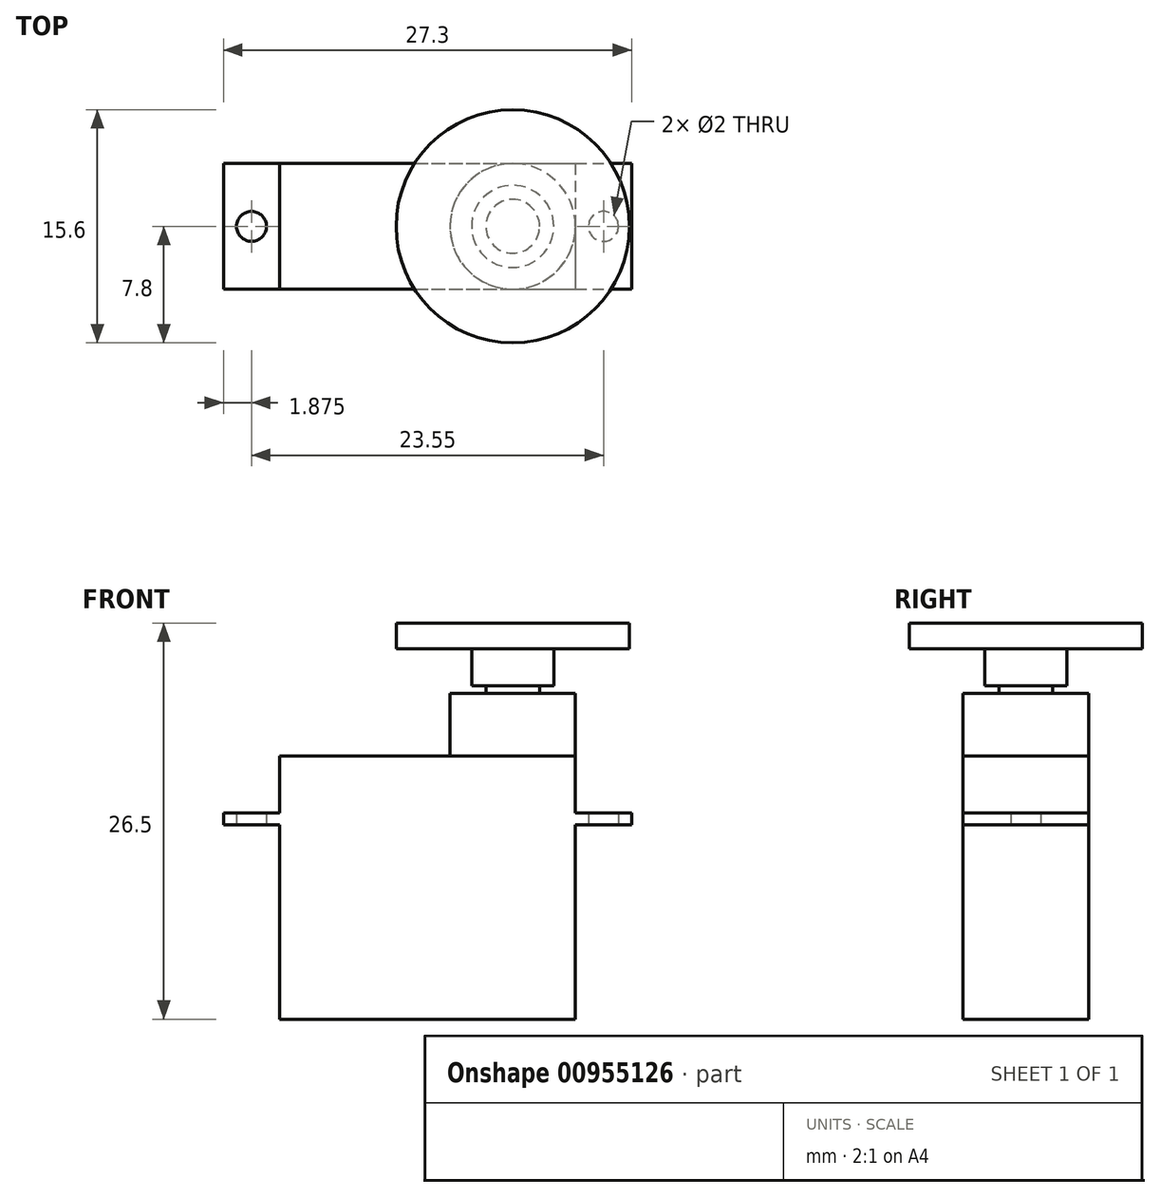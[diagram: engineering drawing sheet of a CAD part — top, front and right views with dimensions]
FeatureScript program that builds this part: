
annotation { "Feature Type Name" : "Feature", "Feature Type Description" : "" }
export const myFeature = defineFeature(function(context is Context, id is Id, definition is map)
    precondition{}
    {
        {
            var Q0;
            Q0=qCreatedBy(makeId("Top.planeOp"),FACE);
            var sketch = newSketch(context, id + "F0", { "sketchPlane" : qUnion([Q0])});
            skLineSegment(sketch, "E0.bottom", {"start": v(-15.6, 4.2) * mm, "end": v(4.2, 4.2) * mm});
            skLineSegment(sketch, "E0.top", {"start": v(-15.6, -4.2) * mm, "end": v(4.2, -4.2) * mm});
            skLineSegment(sketch, "E0.left", {"start": v(-15.6, 4.2) * mm, "end": v(-15.6, -4.2) * mm});
            skLineSegment(sketch, "E0.right", {"start": v(4.2, 4.2) * mm, "end": v(4.2, -4.2) * mm});
            skCircle(sketch, "E1", {"center": v(0, 0) * mm, "radius": 4.2 * mm});
            skCircle(sketch, "E2", {"center": v(0, 0) * mm, "radius": 1.8 * mm});
            skLineSegment(sketch, "E3.bottom", {"start": v(-15.6, 4.2) * mm, "end": v(-19.35, 4.2) * mm});
            skLineSegment(sketch, "E3.top", {"start": v(-15.6, -4.2) * mm, "end": v(-19.35, -4.2) * mm});
            skLineSegment(sketch, "E4", {"start": v(-5.7, 9.97) * mm, "end": v(-5.7, -15.7) * mm, "construction": true});
            skPoint(sketch, "E4.startSnap0", {"position": v(-5.7, 4.2) * mm});
            skLineSegment(sketch, "E5", {"start": v(-19.35, 4.2) * mm, "end": v(-19.35, -4.2) * mm});
            skCircle(sketch, "E6", {"center": v(-17.48, 0) * mm, "radius": 1 * mm});
            skLineSegment(sketch, "E7.MirrorCS", {"start": v(4.2, -4.2) * mm, "end": v(7.95, -4.2) * mm});
            skCircle(sketch, "E8.MirrorC", {"center": v(6.07, 0) * mm, "radius": 1 * mm});
            skLineSegment(sketch, "E9.MirrorCS", {"start": v(4.2, 4.2) * mm, "end": v(7.95, 4.2) * mm});
            skLineSegment(sketch, "E10.MirrorCS", {"start": v(7.95, 4.2) * mm, "end": v(7.95, -4.2) * mm});
            skSolve(sketch);
        }
        {
            var Q0;
            {var subQ0=sQuery(id+"F0.wireOp",EDGE,"E0.left");Q0=makeQuery(id+"F0.imprint","IMPRINT",FACE,{"disambiguationData":[TD([[makeQuery(id+"F0.imprint","IMPRINT",EDGE,{"derivedFrom":subQ0}),1.0]])]});}
            var Q1;
            Q1=makeQuery(id+"F0.imprint","IMPRINT",FACE,{"disambiguationData":[TD([[makeQuery(id+"F0.imprint","IMPRINT",EDGE,{"derivedFrom":sQuery(id+"F0.wireOp",EDGE,"E2")}),-1.0]])]});
            var Q2;
            Q2=makeQuery(id+"F0.imprint","IMPRINT",FACE,{"disambiguationData":[TD([[makeQuery(id+"F0.imprint","IMPRINT",EDGE,{"derivedFrom":sQuery(id+"F0.wireOp",EDGE,"E2")}),1.0]])]});
            var Q3;
            {var subQ1=sQuery(id+"F0.wireOp",EDGE,"E0.bottom");var subQ3=sQuery(id+"F0.wireOp",EDGE,"E1");var subQ4=makeQuery(id+"F0.imprint","INTERSECT",VERTEX,{"derivedFrom":[subQ1,subQ3]});Q3=makeQuery(id+"F0.imprint","IMPRINT",FACE,{"disambiguationData":[TD([[makeQuery(id+"F0.imprint","IMPRINT",EDGE,{"disambiguationData":[TD([[subQ4,1.0]])],"derivedFrom":subQ3}),-1.0]])]});}
            var Q4;
            {var subQ1=sQuery(id+"F0.wireOp",EDGE,"E0.top");var subQ3=sQuery(id+"F0.wireOp",EDGE,"E1");var subQ4=makeQuery(id+"F0.imprint","INTERSECT",VERTEX,{"derivedFrom":[subQ1,subQ3]});Q4=makeQuery(id+"F0.imprint","IMPRINT",FACE,{"disambiguationData":[TD([[makeQuery(id+"F0.imprint","IMPRINT",EDGE,{"disambiguationData":[TD([[subQ4,-1.0]])],"derivedFrom":subQ3}),-1.0]])]});}
            extrude(context, id + "F1", {"entities" : qUnion([Q0, Q1, Q2, Q3, Q4]), "oppositeDirection" : true, "offsetDistance" : 25 * mm, "depth" : 13 * mm, "hasSecondDirection" : true, "secondDirectionOppositeDirection" : false, "secondDirectionDepth" : (17.6 - 13) * mm});
        }
        {
            var Q0;
            Q0=makeQuery(id+"F0.imprint","IMPRINT",FACE,{"disambiguationData":[TD([[makeQuery(id+"F0.imprint","IMPRINT",EDGE,{"derivedFrom":sQuery(id+"F0.wireOp",EDGE,"E3.bottom")}),1.0]])]});
            var Q1;
            {var subQ0=sQuery(id+"F0.wireOp",EDGE,"E7.MirrorCS");Q1=makeQuery(id+"F0.imprint","IMPRINT",FACE,{"disambiguationData":[TD([[makeQuery(id+"F0.imprint","IMPRINT",EDGE,{"derivedFrom":subQ0}),1.0]])]});}
            extrude(context, id + "F2", {"entities" : qUnion([Q0, Q1]), "operationType" : NewBodyOperationType.ADD, "offsetDistance" : 25 * mm, "depth" : 0.8 * mm});
        }
        {
            var Q0;
            Q0=makeQuery(id+"F0.imprint","IMPRINT",FACE,{"disambiguationData":[TD([[makeQuery(id+"F0.imprint","IMPRINT",EDGE,{"derivedFrom":sQuery(id+"F0.wireOp",EDGE,"E2")}),-1.0]])]});
            var Q1;
            Q1=makeQuery(id+"F0.imprint","IMPRINT",FACE,{"disambiguationData":[TD([[makeQuery(id+"F0.imprint","IMPRINT",EDGE,{"derivedFrom":sQuery(id+"F0.wireOp",EDGE,"E2")}),1.0]])]});
            extrude(context, id + "F3", {"entities" : qUnion([Q0, Q1]), "operationType" : NewBodyOperationType.ADD, "offsetDistance" : 25 * mm, "depth" : 8.8 * mm});
        }
        {
            var Q0;
            Q0=makeQuery(id+"F0.imprint","IMPRINT",FACE,{"disambiguationData":[TD([[makeQuery(id+"F0.imprint","IMPRINT",EDGE,{"derivedFrom":sQuery(id+"F0.wireOp",EDGE,"E2")}),1.0]])]});
            extrude(context, id + "F4", {"entities" : qUnion([Q0]), "operationType" : NewBodyOperationType.ADD, "offsetDistance" : 25 * mm, "depth" : (8.8 + 3) * mm});
        }
        {
            var Q0;
            Q0=makeQuery(id+"F4.opExtrude","CAP_FACE",FACE,{"disambiguationData":[OSD([sQuery(id+"F0.wireOp",EDGE,"E2")])],"isStart":false});
            var sketch = newSketch(context, id + "F5", { "sketchPlane" : qUnion([Q0])});
            skCircle(sketch, "E11.0", {"center": v(0, 0) * mm, "radius": 1.8 * mm});
            skCircle(sketch, "E12", {"center": v(0, 0) * mm, "radius": 2.75 * mm});
            skCircle(sketch, "E13", {"center": v(0, 0) * mm, "radius": 7.8 * mm});
            skSolve(sketch);
        }
        {
            var Q0;
            Q0=makeQuery(id+"F5.imprint","IMPRINT",FACE,{"disambiguationData":[TD([[makeQuery(id+"F5.imprint","IMPRINT",EDGE,{"derivedFrom":sQuery(id+"F5.wireOp",EDGE,"E11.0")}),-1.0]])]});
            extrude(context, id + "F6", {"entities" : qUnion([Q0]), "oppositeDirection" : true, "depth" : 2.5 * mm});
        }
        {
            var Q0;
            Q0=makeQuery(id+"F5.imprint","IMPRINT",FACE,{"disambiguationData":[TD([[makeQuery(id+"F5.imprint","IMPRINT",EDGE,{"derivedFrom":sQuery(id+"F5.wireOp",EDGE,"E12")}),-1.0]])]});
            var Q1;
            Q1=makeQuery(id+"F5.imprint","IMPRINT",FACE,{"disambiguationData":[TD([[makeQuery(id+"F5.imprint","IMPRINT",EDGE,{"derivedFrom":sQuery(id+"F5.wireOp",EDGE,"E11.0")}),-1.0]])]});
            var Q2;
            Q2=makeQuery(id+"F5.imprint","IMPRINT",FACE,{"disambiguationData":[TD([[makeQuery(id+"F5.imprint","IMPRINT",EDGE,{"derivedFrom":sQuery(id+"F5.wireOp",EDGE,"E11.0")}),1.0]])]});
            extrude(context, id + "F7", {"entities" : qUnion([Q0, Q1, Q2]), "operationType" : NewBodyOperationType.ADD, "depth" : 1.7 * mm});
        }
    });
